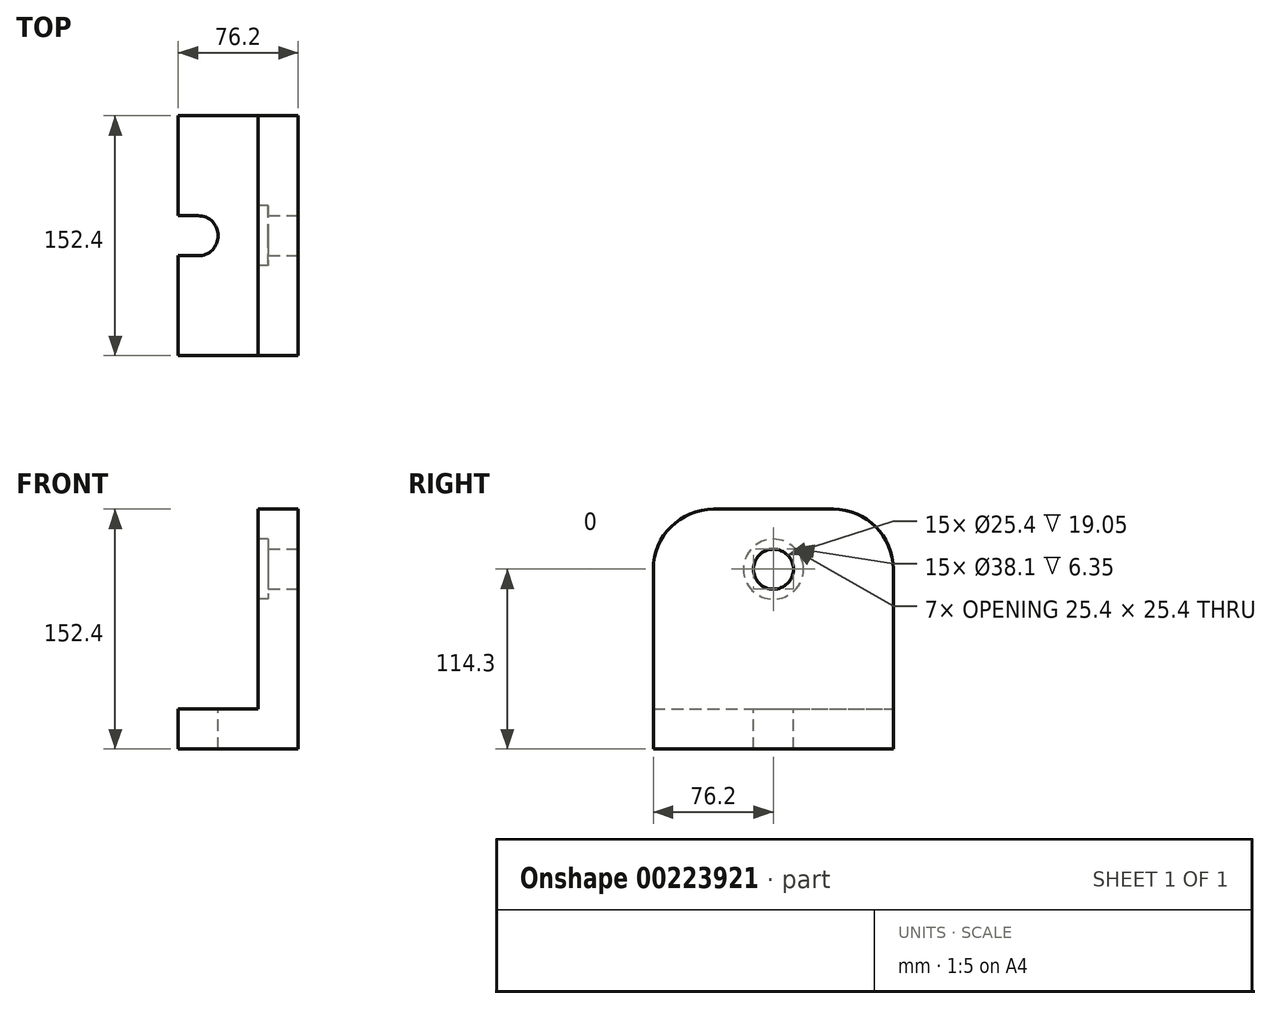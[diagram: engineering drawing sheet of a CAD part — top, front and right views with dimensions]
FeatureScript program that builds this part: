
annotation { "Feature Type Name" : "Feature", "Feature Type Description" : "" }
export const myFeature = defineFeature(function(context is Context, id is Id, definition is map)
    precondition{}
    {
        {
            var Q0;
            Q0=qCreatedBy(makeId("Front.planeOp"),FACE);
            var sketch = newSketch(context, id + "F0", { "sketchPlane" : qUnion([Q0])});
            skLineSegment(sketch, "E0", {"start": v(0, 0) * mm, "end": v(-76.2, 0) * mm});
            skLineSegment(sketch, "E1", {"start": v(-76.2, 0) * mm, "end": v(-76.2, 25.4) * mm});
            skLineSegment(sketch, "E2", {"start": v(-76.2, 25.4) * mm, "end": v(-25.4, 25.4) * mm});
            skLineSegment(sketch, "E3", {"start": v(-25.4, 25.4) * mm, "end": v(-25.4, 152.4) * mm});
            skLineSegment(sketch, "E4", {"start": v(-25.4, 152.4) * mm, "end": v(0, 152.4) * mm});
            skLineSegment(sketch, "E5", {"start": v(0, 152.4) * mm, "end": v(0, 0) * mm});
            skSolve(sketch);
        }
        {
            var Q0;
            Q0=makeQuery(id+"F0.imprint","IMPRINT",FACE,{"disambiguationData":[TD([[makeQuery(id+"F0.imprint","IMPRINT",EDGE,{"derivedFrom":sQuery(id+"F0.wireOp",EDGE,"E0")}),-1.0]])]});
            extrude(context, id + "F1", {"entities" : qUnion([Q0]), "endBound" : BoundingType.SYMMETRIC, "depth" : 152.4 * mm});
        }
        {
            var Q0;
            Q0=qCreatedBy(makeId("Right.planeOp"),FACE);
            var sketch = newSketch(context, id + "F2", { "sketchPlane" : qUnion([Q0])});
            skCircle(sketch, "E6", {"center": v(0, 114.3) * mm, "radius": 12.7 * mm});
            skSolve(sketch);
        }
        {
            var Q0;
            Q0=makeQuery(id+"F2.imprint","IMPRINT",FACE,{"disambiguationData":[TD([[makeQuery(id+"F2.imprint","IMPRINT",EDGE,{"derivedFrom":sQuery(id+"F2.wireOp",EDGE,"E6")}),1.0]])]});
            extrude(context, id + "F3", {"entities" : qUnion([Q0]), "operationType" : NewBodyOperationType.REMOVE, "endBound" : BoundingType.THROUGH_ALL, "oppositeDirection" : true, "depth" : 25.4 * mm});
        }
        {
            var Q0;
            Q0=makeQuery(id+"F1.opExtrude","SWEPT_FACE",FACE,{"disambiguationData":[OSD([sQuery(id+"F0.wireOp",EDGE,"E2")])]});
            var sketch = newSketch(context, id + "F4", { "sketchPlane" : qUnion([Q0])});
            skLineSegment(sketch, "E7.bottom", {"start": v(-76.2, 12.7) * mm, "end": v(-63.5, 12.7) * mm});
            skLineSegment(sketch, "E7.top", {"start": v(-76.2, -12.7) * mm, "end": v(-63.5, -12.7) * mm});
            skLineSegment(sketch, "E7.left", {"start": v(-76.2, 12.7) * mm, "end": v(-76.2, -12.7) * mm});
            skLineSegment(sketch, "E7.right", {"start": v(-63.5, 12.7) * mm, "end": v(-63.5, -12.7) * mm});
            skArc(sketch, "E8", {"start": v(-63.5, -12.7) * mm, "mid": v(-50.8, 0) * mm, "end": v(-63.5, 12.7) * mm});
            skSolve(sketch);
        }
        {
            var Q0;
            Q0 = qSketchRegion(id + "F4", true);
            extrude(context, id + "F5", {"entities" : qUnion([Q0]), "operationType" : NewBodyOperationType.REMOVE, "endBound" : BoundingType.THROUGH_ALL, "oppositeDirection" : true, "depth" : 25.4 * mm});
        }
        {
            var Q0;
            Q0=makeQuery(id+"F1.opExtrude","SWEPT_FACE",FACE,{"disambiguationData":[OSD([sQuery(id+"F0.wireOp",EDGE,"E3")])]});
            var sketch = newSketch(context, id + "F6", { "sketchPlane" : qUnion([Q0])});
            skCircle(sketch, "E9", {"center": v(0, 114.3) * mm, "radius": 19.05 * mm});
            skSolve(sketch);
        }
        {
            var Q0;
            Q0=makeQuery(id+"F1.opExtrude","CAP_EDGE",EDGE,{"disambiguationData":[OSD([sQuery(id+"F0.wireOp",EDGE,"E4")])],"isStart":true});
            var Q1;
            Q1=makeQuery(id+"F1.opExtrude","CAP_EDGE",EDGE,{"disambiguationData":[OSD([sQuery(id+"F0.wireOp",EDGE,"E4")])],"isStart":false});
            fillet(context, id + "F7", {"entities" : qUnion([Q0, Q1]), "radius" : 38.1 * mm, "tangentPropagation" : true, "allowEdgeOverflow" : false});
        }
        {
            var Q0;
            Q0 = qSketchRegion(id + "F6", true);
            extrude(context, id + "F8", {"entities" : qUnion([Q0]), "operationType" : NewBodyOperationType.REMOVE, "oppositeDirection" : true, "depth" : 6.35 * mm});
        }
    });
